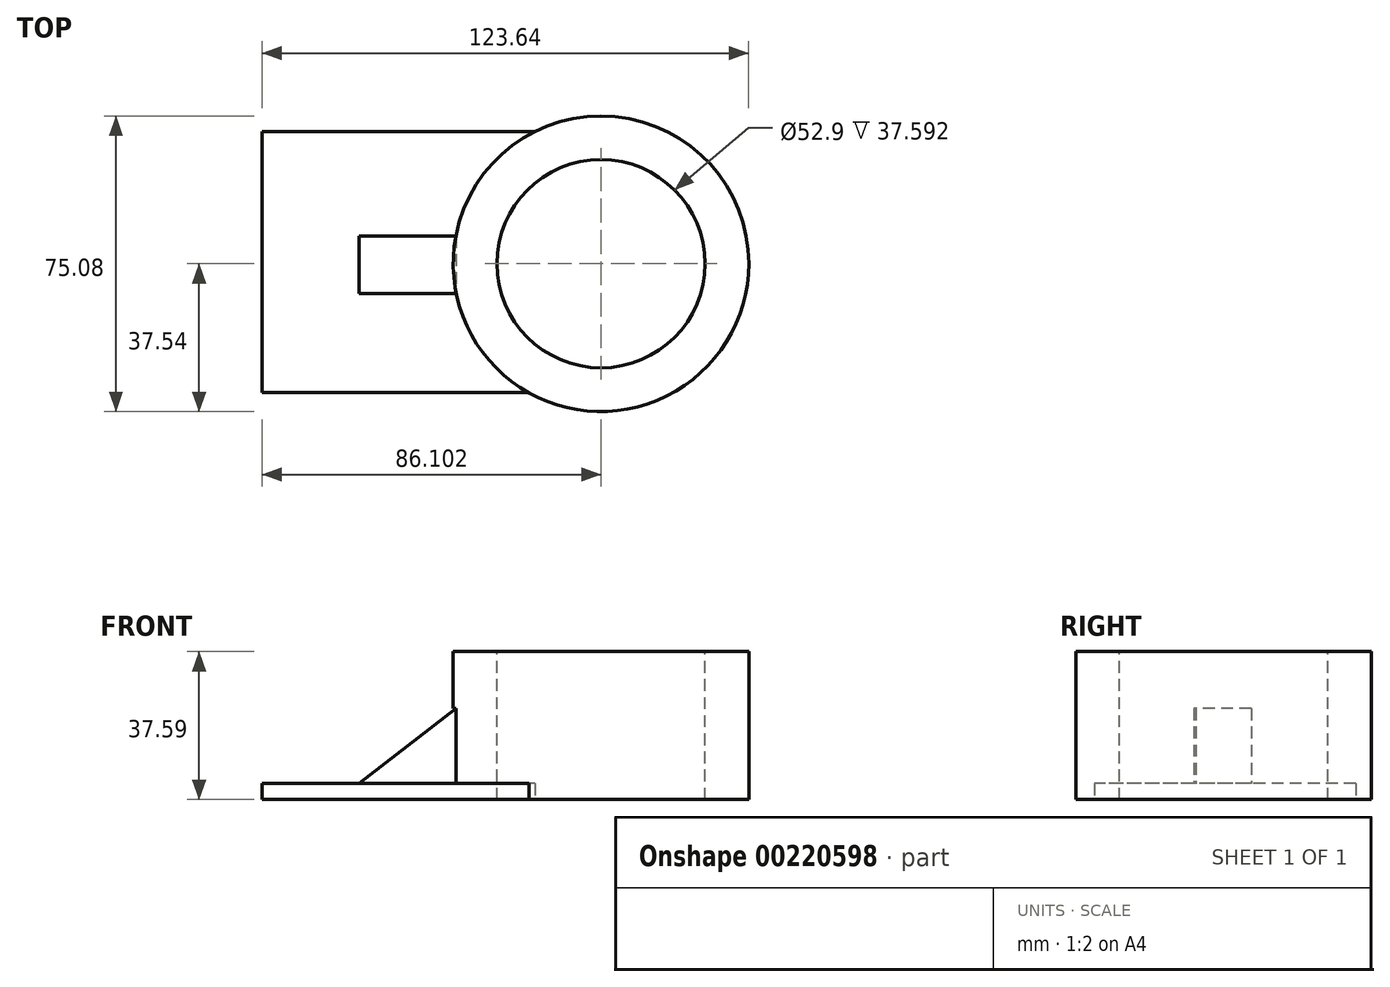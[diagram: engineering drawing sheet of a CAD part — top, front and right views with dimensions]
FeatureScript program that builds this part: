
annotation { "Feature Type Name" : "Feature", "Feature Type Description" : "" }
export const myFeature = defineFeature(function(context is Context, id is Id, definition is map)
    precondition{}
    {
        {
            var Q0;
            Q0=qCreatedBy(makeId("Top.planeOp"),FACE);
            var sketch = newSketch(context, id + "F0", { "sketchPlane" : qUnion([Q0])});
            skCircle(sketch, "E0", {"center": v(21.16, 0) * mm, "radius": 37.54 * mm});
            skSolve(sketch);
        }
        {
            var Q0;
            Q0=makeQuery(id+"F0.imprint","IMPRINT",FACE,{"disambiguationData":[TD([[makeQuery(id+"F0.imprint","IMPRINT",EDGE,{"derivedFrom":sQuery(id+"F0.wireOp",EDGE,"E0")}),1.0]])]});
            extrude(context, id + "F1", {"entities" : qUnion([Q0]), "depth" : 37.6 * mm});
        }
        {
            var Q0;
            Q0=qCreatedBy(makeId("Top.planeOp"),FACE);
            var sketch = newSketch(context, id + "F2", { "sketchPlane" : qUnion([Q0])});
            skLineSegment(sketch, "E1.bottom", {"start": v(4.64, 33.63) * mm, "end": v(-64.94, 33.63) * mm});
            skLineSegment(sketch, "E1.top", {"start": v(4.64, -32.76) * mm, "end": v(-64.94, -32.76) * mm});
            skLineSegment(sketch, "E1.left", {"start": v(4.64, 33.63) * mm, "end": v(4.64, -32.76) * mm});
            skLineSegment(sketch, "E1.right", {"start": v(-64.94, 33.63) * mm, "end": v(-64.94, -32.76) * mm});
            skSolve(sketch);
        }
        {
            var Q0;
            Q0=makeQuery(id+"F2.imprint","IMPRINT",FACE,{"disambiguationData":[TD([[makeQuery(id+"F2.imprint","IMPRINT",EDGE,{"derivedFrom":sQuery(id+"F2.wireOp",EDGE,"E1.bottom")}),1.0]])]});
            extrude(context, id + "F3", {"entities" : qUnion([Q0]), "operationType" : NewBodyOperationType.ADD, "depth" : 4.06 * mm});
        }
        {
            var Q0;
            Q0=makeQuery(id+"F1.opExtrude","CAP_FACE",FACE,{"disambiguationData":[OSD([sQuery(id+"F0.wireOp",EDGE,"E0")])],"isStart":false});
            var sketch = newSketch(context, id + "F4", { "sketchPlane" : qUnion([Q0])});
            skCircle(sketch, "E2", {"center": v(21.16, 0) * mm, "radius": 26.45 * mm});
            skSolve(sketch);
        }
        {
            var Q0;
            Q0=makeQuery(id+"F4.imprint","IMPRINT",FACE,{"disambiguationData":[TD([[makeQuery(id+"F4.imprint","IMPRINT",EDGE,{"derivedFrom":sQuery(id+"F4.wireOp",EDGE,"E2")}),1.0]])]});
            extrude(context, id + "F5", {"entities" : qUnion([Q0]), "operationType" : NewBodyOperationType.REMOVE, "endBound" : BoundingType.THROUGH_ALL, "oppositeDirection" : true, "depth" : 25.4 * mm});
        }
        {
            var Q0;
            Q0=makeQuery(id+"F3.opExtrude","CAP_FACE",FACE,{"disambiguationData":[OSD([sQuery(id+"F2.wireOp",EDGE,"E1.bottom"),sQuery(id+"F2.wireOp",EDGE,"E1.top"),sQuery(id+"F2.wireOp",EDGE,"E1.left"),sQuery(id+"F2.wireOp",EDGE,"E1.right")])],"isStart":false});
            var sketch = newSketch(context, id + "F6", { "sketchPlane" : qUnion([Q0])});
            skLineSegment(sketch, "E3.bottom", {"start": v(-15.71, 7.03) * mm, "end": v(-40.3, 7.03) * mm});
            skLineSegment(sketch, "E3.top", {"start": v(-15.71, -7.54) * mm, "end": v(-40.3, -7.54) * mm});
            skLineSegment(sketch, "E3.left", {"start": v(-15.71, 7.03) * mm, "end": v(-15.71, -7.54) * mm});
            skLineSegment(sketch, "E3.right", {"start": v(-40.3, 7.03) * mm, "end": v(-40.3, -7.54) * mm});
            skSolve(sketch);
        }
        {
            var Q0;
            {var subQ4=sQuery(id+"F6.wireOp",EDGE,"E3.bottom");Q0=makeQuery(id+"F6.imprint","IMPRINT",FACE,{"disambiguationData":[TD([[makeQuery(id+"F6.imprint","IMPRINT",EDGE,{"derivedFrom":subQ4}),1.0]])]});}
            extrude(context, id + "F7", {"entities" : qUnion([Q0]), "operationType" : NewBodyOperationType.ADD, "depth" : 19.05 * mm});
        }
        {
            var Q0;
            Q0=makeQuery(id+"F7.opExtrude","SWEPT_FACE",FACE,{"disambiguationData":[OSD([sQuery(id+"F6.wireOp",EDGE,"E3.top")])]});
            var sketch = newSketch(context, id + "F8", { "sketchPlane" : qUnion([Q0])});
            skLineSegment(sketch, "E4", {"start": v(-40.3, 4.06) * mm, "end": v(-15.71, 23.11) * mm});
            skSolve(sketch);
        }
        {
            var Q0;
            Q0=makeQuery(id+"F8.imprint","IMPRINT",FACE,{"disambiguationData":[TD([[makeQuery(id+"F8.imprint","IMPRINT",EDGE,{"derivedFrom":sQuery(id+"F8.wireOp",EDGE,"E4")}),1.0]])]});
            extrude(context, id + "F9", {"entities" : qUnion([Q0]), "operationType" : NewBodyOperationType.REMOVE, "endBound" : BoundingType.THROUGH_ALL, "oppositeDirection" : true, "depth" : 25.4 * mm});
        }
    });
